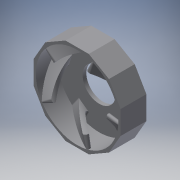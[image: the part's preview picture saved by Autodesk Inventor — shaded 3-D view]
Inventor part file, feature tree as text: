
AUTODESK INVENTOR PART (.ipt)
format: ipt  version: 2017 (Build 210142000, 142)  size: 595,456 bytes
history: native  units: in
note: dims shown in document units (in); Inventor stores cm internally (conversion verified against a paired STEP export)
features: sketch x3, extrude x2, fillet x2, helix x1, pattern_circular x1, projected_geometry x1
ambient origin geometry x8: Origin, YZ Plane, XZ Plane, XY Plane, X Axis, Y Axis, Z Axis, Center Point
bodies: Solid1 (feature_tree)
feature tree (10):
  extrude  "Extrusion1"  Depth=0.75in TaperAngle=0.0deg
  extrude  "Extrusion2"  Depth=0.12in
  helix  "Coil1"  [1 undecoded]
  fillet  "Fillet1"  Radius=0.0625in
  fillet  "Fillet2"  Radius=2.95in
  pattern_circular  "Circular Pattern2"  [2 undecoded]
  sketch  "Sketch1"  dims[d0=0.125in d1=0.0in d2=0.75in d3=0.0in]
  sketch  "Sketch2"  dims[d4=0.12in d5=0.12in d6=1.0in]
  projected_geometry  "Projected Loop1"
  sketch  "Sketch3"  dims[d7=5.0in d8=0.75in d9=0.3937in d10=0.0in d11=90.0deg d12=90.0deg d13=0.0in d14=0.0in d15=0.0625in d19=2.95in d20=1.125in d21=2.8in d22=0.0625in d23=1.9685in d24=360.0deg d26=0.45in]
note: 3 required parameter values undecoded (feature->parameter linkage not recoverable at this tier; creation-order binding heuristic only, values carry confidence <= 0.55)
